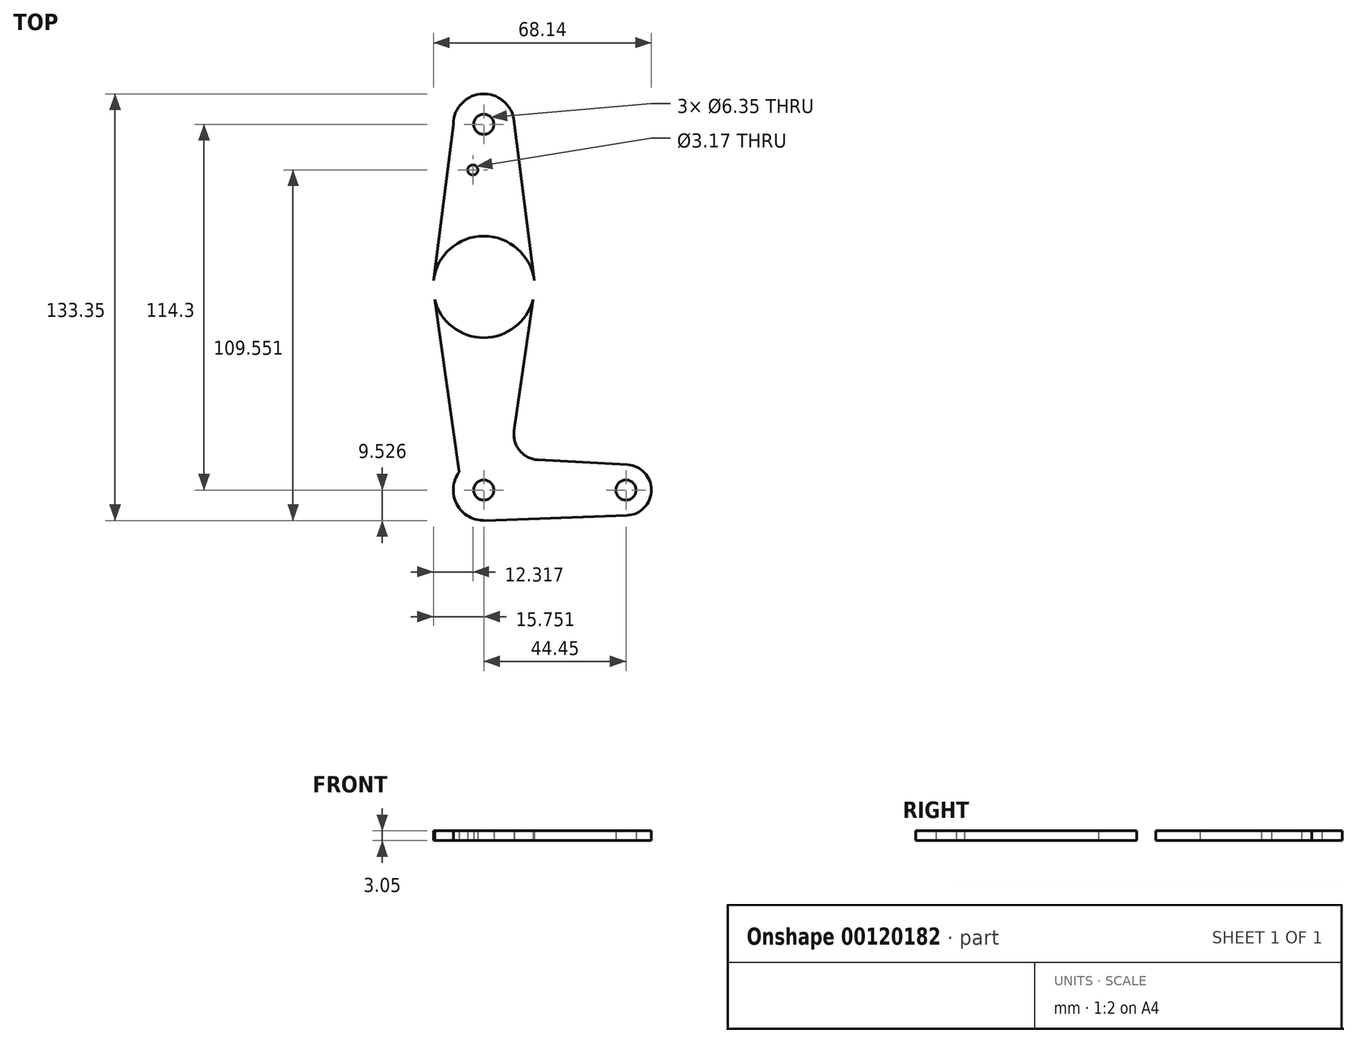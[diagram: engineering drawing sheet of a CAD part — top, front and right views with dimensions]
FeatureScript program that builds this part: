
annotation { "Feature Type Name" : "Feature", "Feature Type Description" : "" }
export const myFeature = defineFeature(function(context is Context, id is Id, definition is map)
    precondition{}
    {
        {
            var Q0;
            Q0=qCreatedBy(makeId("Top.planeOp"),FACE);
            var sketch = newSketch(context, id + "F0", { "sketchPlane" : qUnion([Q0])});
            skCircle(sketch, "E0", {"center": v(-102.44, 51.76) * mm, "radius": 9.53 * mm});
            skLineSegment(sketch, "E1", {"start": v(-102.44, 51.76) * mm, "end": v(-102.44, -62.54) * mm});
            skCircle(sketch, "E2", {"center": v(-102.44, -62.54) * mm, "radius": 9.53 * mm});
            skLineSegment(sketch, "E3", {"start": v(-102.44, -62.54) * mm, "end": v(-57.99, -62.54) * mm});
            skCircle(sketch, "E4", {"center": v(-102.44, 0.96) * mm, "radius": 1.59 * mm});
            skCircle(sketch, "E5", {"center": v(-102.44, 0.96) * mm, "radius": 15.88 * mm});
            skLineSegment(sketch, "E6", {"start": v(-111.96, 51.76) * mm, "end": v(-118.19, 2.96) * mm});
            skLineSegment(sketch, "E7", {"start": v(-92.91, 51.76) * mm, "end": v(-86.7, 2.96) * mm});
            skLineSegment(sketch, "E8", {"start": v(-87.06, -3) * mm, "end": v(-92.95, -44.04) * mm});
            skLineSegment(sketch, "E9", {"start": v(-117.81, -3) * mm, "end": v(-110.09, -56.87) * mm});
            skCircle(sketch, "E10", {"center": v(-57.99, -62.54) * mm, "radius": 7.94 * mm});
            skLineSegment(sketch, "E11", {"start": v(-85.5, -53.1) * mm, "end": v(-57.56, -54.62) * mm});
            skLineSegment(sketch, "E12", {"start": v(-102.1, -72.06) * mm, "end": v(-57.7, -70.48) * mm});
            skCircle(sketch, "E13", {"center": v(-105.87, 37.48) * mm, "radius": 1.59 * mm});
            skPoint(sketch, "E14.newPointA", {"position": v(-94.79, -56.87) * mm});
            skArc(sketch, "E14.filletArc", {"start": v(-92.95, -44.04) * mm, "mid": v(-91.23, -50.21) * mm, "end": v(-85.5, -53.1) * mm});
            skCircle(sketch, "E15", {"center": v(-102.44, 51.76) * mm, "radius": 3.18 * mm});
            skCircle(sketch, "E16", {"center": v(-102.44, 0.96) * mm, "radius": 3.18 * mm});
            skCircle(sketch, "E17", {"center": v(-102.44, -62.54) * mm, "radius": 3.18 * mm});
            skCircle(sketch, "E18", {"center": v(-57.99, -62.54) * mm, "radius": 3.18 * mm});
            skSolve(sketch);
        }
        {
            var Q0;
            {var subQ5=sQuery(id+"F0.wireOp",EDGE,"E8");Q0=makeQuery(id+"F0.imprint","IMPRINT",FACE,{"disambiguationData":[TD([[makeQuery(id+"F0.imprint","IMPRINT",EDGE,{"derivedFrom":subQ5}),-1.0]])]});}
            var Q1;
            {var subQ5=sQuery(id+"F0.wireOp",EDGE,"E9");Q1=makeQuery(id+"F0.imprint","IMPRINT",FACE,{"disambiguationData":[TD([[makeQuery(id+"F0.imprint","IMPRINT",EDGE,{"derivedFrom":subQ5}),1.0]])]});}
            var Q2;
            {var subQ0=sQuery(id+"F0.wireOp",EDGE,"E2");var subQ5=sQuery(id+"F0.wireOp",EDGE,"E1");var subQ6=makeQuery(id+"F0.imprint","INTERSECT",VERTEX,{"derivedFrom":[subQ5,subQ0]});Q2=makeQuery(id+"F0.imprint","IMPRINT",FACE,{"disambiguationData":[TD([[makeQuery(id+"F0.imprint","IMPRINT",EDGE,{"disambiguationData":[TD([[subQ6,-1.0]])],"derivedFrom":subQ5}),-1.0]])]});}
            var Q3;
            {var subQ0=sQuery(id+"F0.wireOp",EDGE,"E12");Q3=makeQuery(id+"F0.imprint","IMPRINT",FACE,{"disambiguationData":[TD([[makeQuery(id+"F0.imprint","IMPRINT",EDGE,{"derivedFrom":subQ0}),1.0]])]});}
            var Q4;
            {var subQ0=sQuery(id+"F0.wireOp",EDGE,"E2");var subQ1=sQuery(id+"F0.wireOp",EDGE,"E1");var subQ2=makeQuery(id+"F0.imprint","INTERSECT",VERTEX,{"derivedFrom":[subQ1,subQ0]});Q4=makeQuery(id+"F0.imprint","IMPRINT",FACE,{"disambiguationData":[TD([[makeQuery(id+"F0.imprint","IMPRINT",EDGE,{"disambiguationData":[TD([[subQ2,-1.0]])],"derivedFrom":subQ1}),1.0]])]});}
            var Q5;
            Q5=makeQuery(id+"F0.imprint","IMPRINT",FACE,{"disambiguationData":[TD([[makeQuery(id+"F0.imprint","IMPRINT",EDGE,{"derivedFrom":sQuery(id+"F0.wireOp",EDGE,"E18")}),-1.0]])]});
            var Q6;
            {var subQ0=sQuery(id+"F0.wireOp",EDGE,"E5");var subQ2=sQuery(id+"F0.wireOp",EDGE,"E1");var subQ7=makeQuery(id+"F0.imprint","INTERSECT",VERTEX,{"disambiguationData":[OD(0.0)],"derivedFrom":[subQ2,subQ0]});Q6=makeQuery(id+"F0.imprint","IMPRINT",FACE,{"disambiguationData":[TD([[makeQuery(id+"F0.imprint","IMPRINT",EDGE,{"disambiguationData":[TD([[subQ7,-1.0]])],"derivedFrom":subQ2}),1.0]])]});}
            var Q7;
            {var subQ0=sQuery(id+"F0.wireOp",EDGE,"E5");var subQ3=sQuery(id+"F0.wireOp",EDGE,"E1");var subQ4=makeQuery(id+"F0.imprint","INTERSECT",VERTEX,{"disambiguationData":[OD(0.0)],"derivedFrom":[subQ3,subQ0]});Q7=makeQuery(id+"F0.imprint","IMPRINT",FACE,{"disambiguationData":[TD([[makeQuery(id+"F0.imprint","IMPRINT",EDGE,{"disambiguationData":[TD([[subQ4,-1.0]])],"derivedFrom":subQ3}),-1.0]])]});}
            var Q8;
            {var subQ0=sQuery(id+"F0.wireOp",EDGE,"E6");Q8=makeQuery(id+"F0.imprint","IMPRINT",FACE,{"disambiguationData":[TD([[makeQuery(id+"F0.imprint","IMPRINT",EDGE,{"derivedFrom":subQ0}),1.0]])]});}
            var Q9;
            {var subQ0=sQuery(id+"F0.wireOp",EDGE,"E7");Q9=makeQuery(id+"F0.imprint","IMPRINT",FACE,{"disambiguationData":[TD([[makeQuery(id+"F0.imprint","IMPRINT",EDGE,{"derivedFrom":subQ0}),-1.0]])]});}
            var Q10;
            Q10=makeQuery(id+"F0.imprint","IMPRINT",FACE,{"disambiguationData":[TD([[makeQuery(id+"F0.imprint","IMPRINT",EDGE,{"derivedFrom":sQuery(id+"F0.wireOp",EDGE,"E15")}),-1.0]])]});
            extrude(context, id + "F1", {"entities" : qUnion([Q0, Q1, Q2, Q3, Q4, Q5, Q6, Q7, Q8, Q9, Q10]), "depth" : 3.05 * mm});
        }
    });
